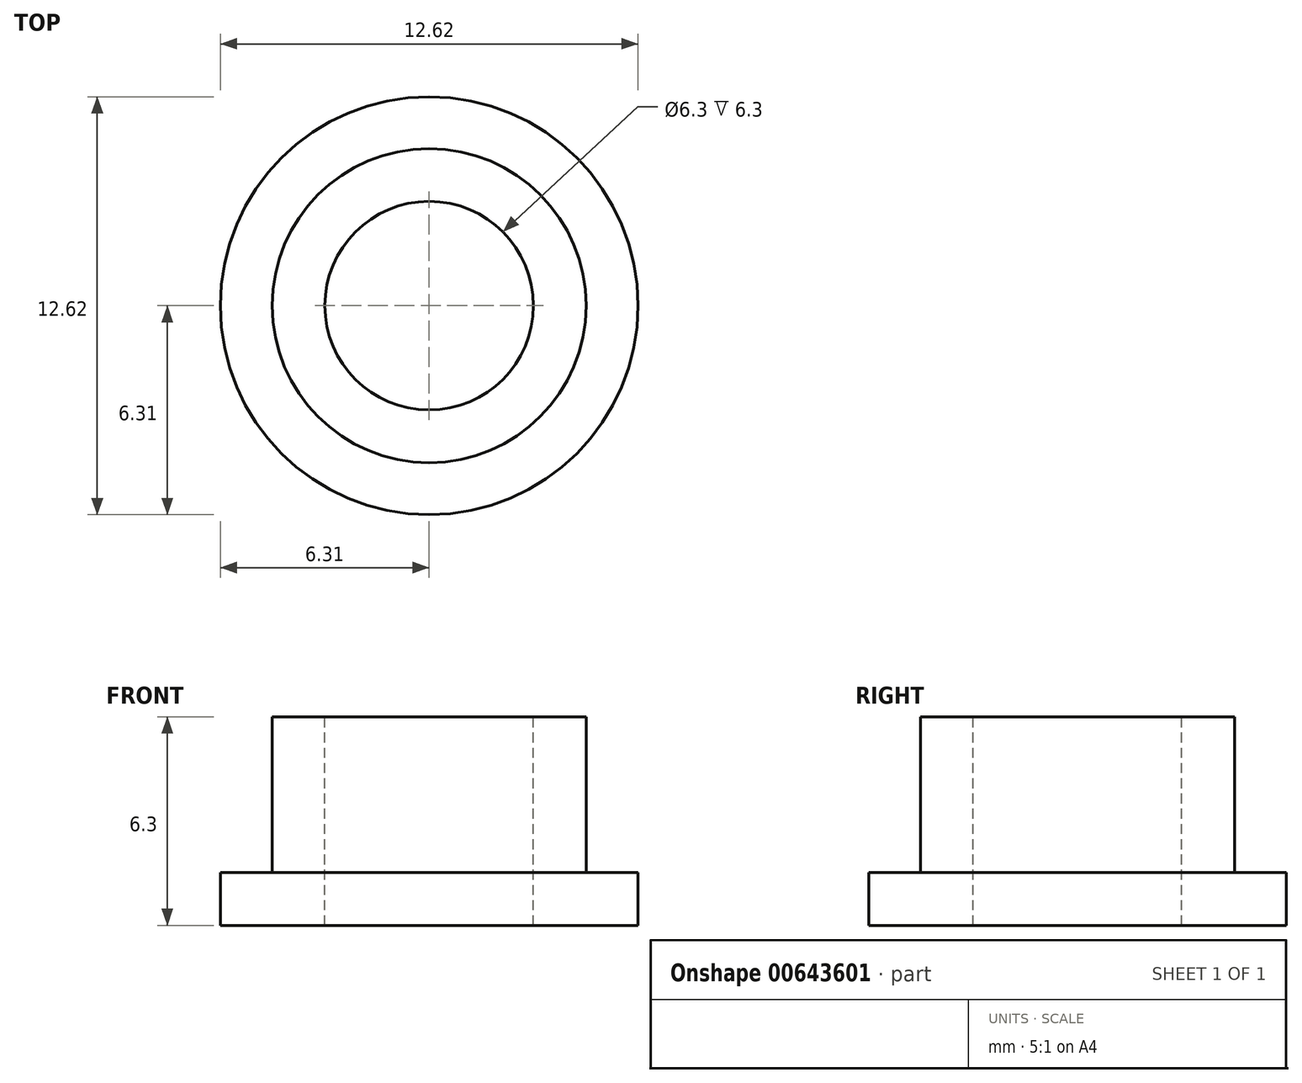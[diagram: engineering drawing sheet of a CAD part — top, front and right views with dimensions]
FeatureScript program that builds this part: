
annotation { "Feature Type Name" : "Feature", "Feature Type Description" : "" }
export const myFeature = defineFeature(function(context is Context, id is Id, definition is map)
    precondition{}
    {
        {
            var Q0;
            Q0=qCreatedBy(makeId("Top.planeOp"),FACE);
            var sketch = newSketch(context, id + "F0", { "sketchPlane" : qUnion([Q0])});
            skCircle(sketch, "E0", {"center": v(0, 0) * mm, "radius": 6.31 * mm});
            skSolve(sketch);
        }
        {
            var Q0;
            Q0 = qSketchRegion(id + "F0", true);
            extrude(context, id + "F1", {"entities" : qUnion([Q0]), "depth" : 1.59 * mm, "offsetDistance" : 25 * mm});
        }
        {
            var Q0;
            Q0=makeQuery(id+"F1.opExtrude","CAP_FACE",FACE,{"disambiguationData":[OSD([sQuery(id+"F0.wireOp",EDGE,"E0")])],"isStart":false});
            var sketch = newSketch(context, id + "F2", { "sketchPlane" : qUnion([Q0])});
            skCircle(sketch, "E1", {"center": v(0, 0) * mm, "radius": 3.15 * mm});
            skSolve(sketch);
        }
        {
            var Q0;
            Q0=makeQuery(id+"F2.imprint","IMPRINT",FACE,{"disambiguationData":[TD([[makeQuery(id+"F2.imprint","IMPRINT",EDGE,{"derivedFrom":sQuery(id+"F2.wireOp",EDGE,"E1")}),1.0]])]});
            extrude(context, id + "F3", {"entities" : qUnion([Q0]), "operationType" : NewBodyOperationType.REMOVE, "endBound" : BoundingType.THROUGH_ALL, "oppositeDirection" : true, "depth" : 25 * mm, "offsetDistance" : 25 * mm});
        }
        {
            var Q0;
            Q0=makeQuery(id+"F1.opExtrude","CAP_FACE",FACE,{"disambiguationData":[OSD([sQuery(id+"F0.wireOp",EDGE,"E0")])],"isStart":false});
            var sketch = newSketch(context, id + "F4", { "sketchPlane" : qUnion([Q0])});
            skCircle(sketch, "E2", {"center": v(0, 0) * mm, "radius": 4.74 * mm});
            skSolve(sketch);
        }
        {
            var Q0;
            Q0=makeQuery(id+"F4.imprint","IMPRINT",FACE,{"disambiguationData":[TD([[makeQuery(id+"F4.imprint","IMPRINT",EDGE,{"derivedFrom":sQuery(id+"F4.wireOp",EDGE,"E2")}),1.0]])]});
            extrude(context, id + "F5", {"entities" : qUnion([Q0]), "operationType" : NewBodyOperationType.ADD, "depth" : 4.7 * mm, "offsetDistance" : 25 * mm});
        }
    });
